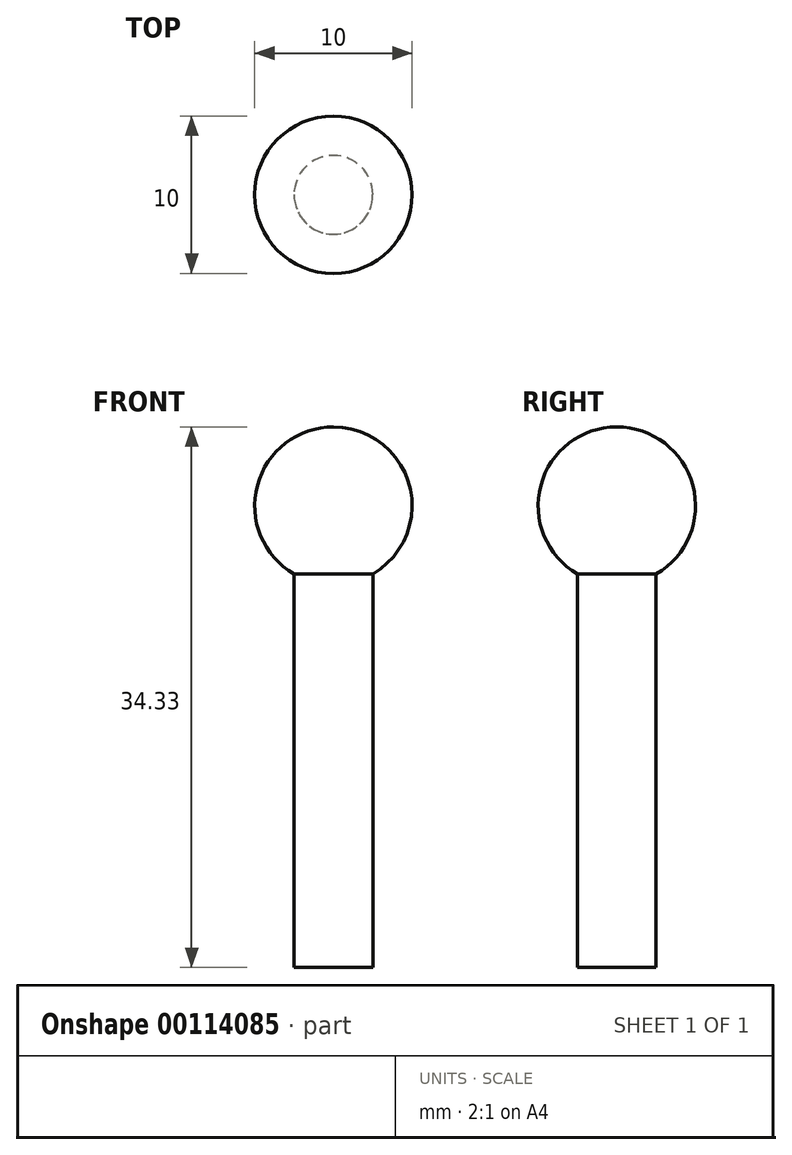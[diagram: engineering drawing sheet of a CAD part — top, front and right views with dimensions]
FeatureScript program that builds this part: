
annotation { "Feature Type Name" : "Feature", "Feature Type Description" : "" }
export const myFeature = defineFeature(function(context is Context, id is Id, definition is map)
    precondition{}
    {
        {
            var Q0;
            Q0=qCreatedBy(makeId("Front.planeOp"),FACE);
            var sketch = newSketch(context, id + "F0", { "sketchPlane" : qUnion([Q0])});
            skLineSegment(sketch, "E0", {"start": v(0, 0) * mm, "end": v(0, 34.33) * mm});
            skLineSegment(sketch, "E1", {"start": v(0, 0) * mm, "end": v(2.5, 0) * mm});
            skLineSegment(sketch, "E2", {"start": v(2.5, 0) * mm, "end": v(2.5, 25) * mm});
            skArc(sketch, "E3", {"start": v(2.5, 25) * mm, "mid": v(4.83, 30.62) * mm, "end": v(0, 34.33) * mm});
            skSolve(sketch);
        }
        {
            var Q0;
            Q0 = qSketchRegion(id + "F0", true);
            var Q1;
            Q1=sQuery(id+"F0.wireOp",EDGE,"E0");
            revolve(context, id + "F1", {"entities" : qUnion([Q0]), "axis" : qUnion([Q1]), "revolveType" : RevolveType.FULL});
        }
    });
